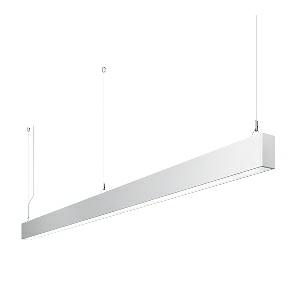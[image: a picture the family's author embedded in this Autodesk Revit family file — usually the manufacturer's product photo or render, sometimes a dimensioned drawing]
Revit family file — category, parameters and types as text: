
# Revit family: idoo_line_-_ilp_6000_vtl_d_00806456_65e3
name_source: partatom
category: Lighting Fixtures
units: mm (PartAtom-declared; Revit-internal decimal feet)

## family parameters
Cut with Voids When Loaded = No
Host = Face
Light Source = No
Part Type = Normal
Room Calculation Point = No
Round Connector Dimension = Use Diameter
Shared = No

## types (1)
- IDOO.line - ILP 6000/VTL/D (1 x LED, 6150 lm, 2700-6500K)
    Apparent Load = 63 VA
    Approval mark = CE
    CIE Flux Codes = 66 91 98 40 100
    Color Rendering = 90-100
    Color Temperature = 2700-6500K
    Control Gear = Electronic ballast
    Default Elevation = 1800 mm
    Description = ILP 6000/VTL/D|Suspended luminaire|light source: LED|connected load: 220-240 V, 50/60 Hz|Power consumption: approx. 63 W|standby: approx. 0,25|luminous flux: 6150 lm|luminous efficacy: 97 lm/W|light distribution: Direct/indirect|direct ratio: approx. 40 %|colour temperature: Cold white, ca. 2700-6500 K|color rendering index (CRI): >= 90|chromaticity tolerance:  3 SDCM|System of protection: IP 40|technology: Continuously dimmable|luminaire body|material: Sectional aluminium|colour: White|lamp cover: Acrylic (PMMA), Clear|mains lead: 2.00 m With free stranded wires|Fastening: Steel cable 0.3 - 0.7 m|glare control: Prism aperture|luminance(L65): <= 2700 cd/m|unified glare rating(4H 8H): <=  16|special features: Specified values at approx. 4000 K, DALI Load 1x, External control required for Dali Device type 8, Flicker-free, Constant luminous flux between 2700 and 6500 K, Constant colour temperature over the whole dimming range, Suitable as emergency lighting|
    Frequency = 50 Hz
    Height = 110 mm
    Lamp = 1 x LED
    Lamp Light Flux = 6150 lm
    Lamp count = 1
    Length = 2256 mm
    Luminous efficacy = 98 lm/W
    Manufacturer = Waldmann
    ModVariant = No
    Model = 00806456
    Mounting Place = Ceiling
    Mounting Type = Pendant
    Number of Poles = 1
    OnlyDefault = Yes
    Power Factor = 1
    Product Name = IDOO.line - ILP 6000/VTL/D
    Product group = Suspended luminaire
    ProductGroupID = 9
    Protection Class = Protection class I
    Protection Degree = IP 40
    RLX_Detail_Level = 1
    RLX_Emergency_Light_Flux = 0 lm
    RLX_Emergency_Type = 0
    RLX_Emergency_Type_DB = No
    RlxData = <blob elided: 21525 chars, md5=5efce3ae>
    Socket = socket
    Standby Power = 0 W
    System Light Flux = 6150 lm
    System Power = 63 W
    Type Comments = Product without accessories
    Type Image = 113293000-00692530.jpg
    URL = http://relux.com
    VarID = ---
    Voltage = 230 V
    Voltage Range = 220-240 V
    Weight = 0.00 kg
    Width = 60 mm  [stored 0.19685 ft]

note: [stored X ft] marks values corroborated as IEEE doubles in the binary element streams (Revit-internal decimal feet)

## geometry (parser evidence)
native form markers: Blend x4, Sweep x14
no freeform markers — native parametric forms only
